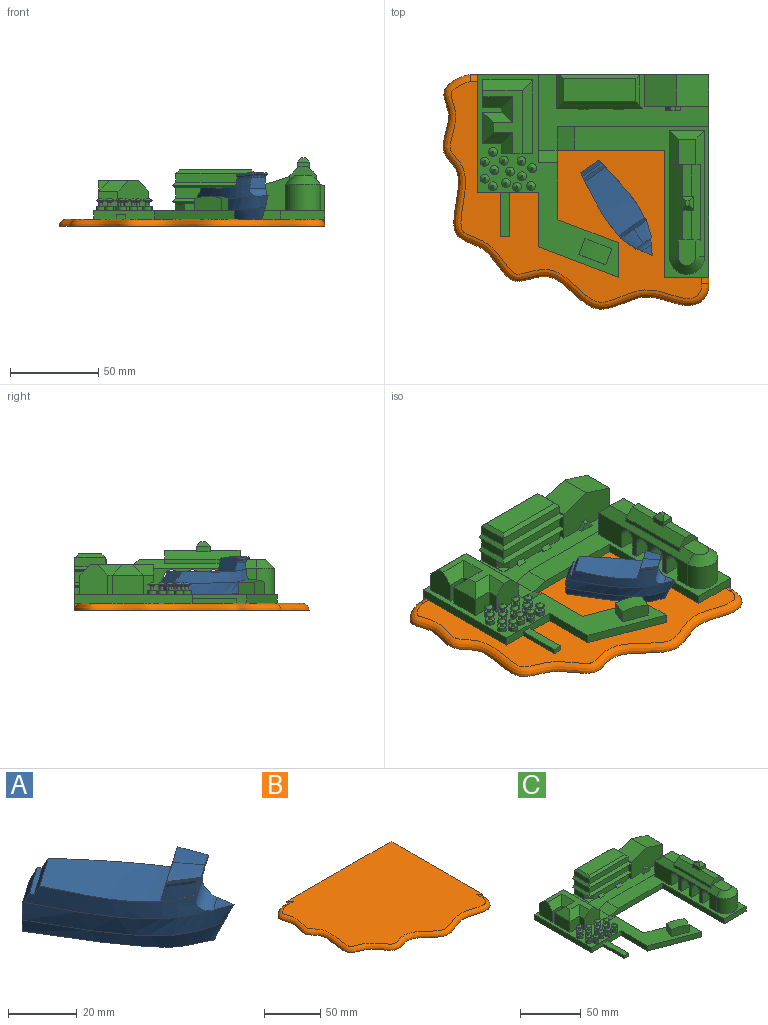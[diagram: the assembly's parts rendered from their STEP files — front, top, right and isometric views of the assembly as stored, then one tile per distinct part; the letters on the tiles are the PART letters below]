
ASSEMBLY  parts=3 mates=4
PART A: 27 faces, bbox 44x56.7x27 mm
  f0: extruded ~48.69x42.18mm, area 653.8mm2, adj f1,f2,f8,f15,f18,f19,f20
  f1: extruded ~10.02x5.16mm, area 44.1mm2, adj f0,f8,f13,f14,f15
  f2: extruded ~44.76x29.14mm, area 304.2mm2, adj f0,f3,f8,f9,f16,f17,f18
  f3: bspline ~54.16x30.25mm, area 415.7mm2, adj f2,f4,f6,f7,f9,f17,f21
  f4: bspline ~51.91x29.86mm, area 327mm2, adj f3,f5,f6,f22
  f5: plane 49.08x36.66mm, normal (0,0,-1), area 618.9mm2, adj f4,f6,f22
  f6: plane 10.3x10.22mm, normal (-0.57,0.82,0), area 123.4mm2, adj f3,f4,f5,f17,f21,f22
  f7: extruded ~8.5x8.26mm, area 17.4mm2, adj f3,f9,f21
  f8: plane 9.48x6.67mm, normal (0.57,-0.82,0), area 63.7mm2, adj f0,f1,f2,f9,f13,f19,f20,f25
  f9: cylinder r=4.5mm len=12.18mm, axis (-0.82,-0.57,0), area 70.7mm2, adj f2,f3,f7,f8,f20,f21
  f10: plane 9.4x6.6mm, normal (0.57,-0.82,0), area 9.7mm2, adj f11,f12,f13,f23,f24,f25
  f11: bspline ~13.1x10.25mm, area 70.7mm2, adj f10,f12,f15,f23
  f12: plane 10.05x3mm, normal (0.96,0.29,0), area 8.3mm2, adj f10,f11,f14,f15
  f13: bspline ~6.43x5.17mm, area 16.8mm2, adj f1,f8,f10,f14,f25
  f14: bspline ~10.67x3.88mm, area 18.7mm2, adj f1,f12,f13,f15
  f15: plane 15.46x11.63mm, normal (-0.56,0.79,0.25), area 138.5mm2, adj f0,f1,f11,f12,f14,f19,f23,f24
  f16: plane 11.87x8.91mm, normal (0,0,1), area 19.2mm2, adj f2,f17,f18,f20
  f17: plane 11.89x9.26mm, normal (-0.51,0.73,0.45), area 65mm2, adj f2,f3,f6,f16,f20,f21
  f18: plane 12.46x9.45mm, normal (-0.51,0.73,0.45), area 54.1mm2, adj f0,f2,f16,f20
  f19: extruded ~8.43x6.13mm, area 44.1mm2, adj f0,f8,f15,f25,f26
  f20: extruded ~42.69x32.09mm, area 304.2mm2, adj f0,f8,f9,f16,f17,f18,f21
  f21: bspline ~46.95x40.55mm, area 415.7mm2, adj f3,f6,f7,f9,f17,f20,f22
  f22: bspline ~45.06x39.16mm, area 327mm2, adj f4,f5,f6,f21
  f23: bspline ~12.9x11.24mm, area 70.7mm2, adj f10,f11,f15,f24
  f24: plane 8.42x6.26mm, normal (-0.6,-0.8,0), area 8.3mm2, adj f10,f15,f23,f26
  f25: bspline ~6.27x5.23mm, area 16.7mm2, adj f8,f10,f13,f19,f26
  f26: bspline ~9.37x7.07mm, area 18.5mm2, adj f15,f19,f24,f25
PART B: 9 faces, bbox 153.8x135.9x5.9 mm
  f0: plane 5.47x5.47mm, normal (-0.66,-0.75,0), area 4.6mm2, adj f1,f4,f6
  f1: plane 146.8x128.87mm, normal (0,0,1), area 16367.4mm2, adj f0,f2,f3,f4,f6,f7,f8
  f2: plane 6.5x5.92mm, normal (-0.66,-0.75,0), area 5.2mm2, adj f1,f3,f7
  f3: plane 131.21x4mm, normal (0,1,0), area 524.9mm2, adj f1,f2,f4,f5
  f4: plane 114.76x4mm, normal (1,0,0), area 459mm2, adj f0,f1,f3,f5
  f5: plane 151.91x133.98mm, normal (0,0,-1), area 17455.2mm2, adj f3,f4,f6,f7,f8
  f6: cylinder r=4mm len=6.98mm, axis (0,1,0), area 32.8mm2, adj f0,f1,f5,f8
  f7: cylinder r=4mm len=8.72mm, axis (1,0,0), area 40.4mm2, adj f1,f2,f5,f8
  f8: bspline ~150.81x132.87mm, area 1645.3mm2, adj f1,f5,f6,f7
PART C: 222 faces, bbox 131.2x114.8x35 mm
  f0: plane 25x5.22mm, normal (0,0,1), area 130.4mm2, adj f1,f3,f4,f5
  f1: plane 25x2.74mm, normal (-1,0,0), area 68.5mm2, adj f0,f2,f4,f5
  f2: plane 131.21x114.76mm, normal (0,0,-1), area 9680.6mm2, adj f1,f3,f4,f5,f14,f18,f19,f21
  f3: plane 25x2.74mm, normal (1,0,0), area 68.5mm2, adj f0,f2,f4,f5
  f4: plane 5.22x2.74mm, normal (0,-1,0), area 14.3mm2, adj f0,f1,f2,f3
  f5: plane 34.32x5mm, normal (0,-1,0), area 157.3mm2, adj f0,f1,f2,f3,f21,f27,f28
  f6: plane 9.07x6.93mm, normal (0.93,-0.35,0), area 67.2mm2, adj f7,f28,f40,f221
  f7: plane 15.35x8mm, normal (-0.35,-0.93,0), area 125.5mm2, adj f6,f28,f41,f221
  f8: plane 17.31x6mm, normal (-1,0,0), area 103.9mm2, adj f9,f14,f198,f204
  f9: plane 45.1x6mm, normal (0,-1,0), area 270.6mm2, adj f8,f10,f199,f205
  f10: plane 17.31x6mm, normal (1,0,0), area 103.9mm2, adj f9,f14,f200,f206
  f11: plane 16.56x6.5mm, normal (-1,0,0), area 82.2mm2, adj f14,f20,f203,f207,f212
  f12: plane 44.35x6.5mm, normal (0,-1,0), area 240.3mm2, adj f13,f20,f202,f207,f212,f213,f214,f215
  f13: plane 17.31x6.5mm, normal (1,0,0), area 112.5mm2, adj f12,f14,f20,f201
  f14: plane 131.21x26mm, normal (0,1,0), area 2190.5mm2, adj f2,f8,f10,f11,f13,f18,f20,f26
  f15: plane 71.57x15mm, normal (1,0,0), area 604.2mm2, adj f43,f56,f58,f63,f81,f82,f83,f84
  f16: plane 16.99x4.99mm, normal (0,0,1), area 84.8mm2, adj f48,f53,f67,f68
  f17: plane 14.6x9.99mm, normal (0,0,1), area 145.8mm2, adj f51,f63,f65,f66
  f18: plane 114.76x19mm, normal (1,0,0), area 794.4mm2, adj f2,f14,f20,f42,f43,f45,f60,f186
  f19: plane 60.93x5mm, normal (0,-1,0), area 291.5mm2, adj f2,f25,f43,f44,f61,f62
  f20: plane 96.9x42.81mm, normal (0,0,1), area 1511.6mm2, adj f11,f12,f13,f14,f18,f26,f42,f60
  f21: plane 30.82x5mm, normal (-1,0,0), area 154.1mm2, adj f2,f5,f22,f28
  f22: plane 45.51x17.26mm, normal (-0.35,-0.93,0), area 243.4mm2, adj f2,f21,f23,f28
  f23: plane 19.59x5mm, normal (1,0,0), area 97.9mm2, adj f2,f22,f24,f28
  f24: plane 34.47x13.08mm, normal (0.35,0.93,0), area 184.3mm2, adj f2,f23,f25,f28
  f25: plane 39.29x5mm, normal (1,0,0), area 187.7mm2, adj f2,f19,f24,f28,f62
  f26: plane 49.81x2.5mm, normal (1,0,0), area 115.8mm2, adj f14,f20,f28,f62
  f27: plane 66.67x5mm, normal (-1,0,0), area 333.4mm2, adj f2,f5,f14,f28
  f28: plane 114.76x79.83mm, normal (0,0,1), area 2011.8mm2, adj f5,f6,f7,f14,f21,f22,f23,f24
  f29: plane 17x15.69mm, normal (-1,0,0), area 230.7mm2, adj f28,f30,f38,f39,f74,f75
  f30: plane 11x10.83mm, normal (0,-1,0), area 119.1mm2, adj f28,f29,f31,f75
  f31: plane 11x2.65mm, normal (-1,0,0), area 29.2mm2, adj f28,f30,f32,f76
  f32: plane 11x10.83mm, normal (0,1,0), area 119.1mm2, adj f28,f31,f33,f77
  f33: plane 17.5x11mm, normal (-1,0,0), area 192.5mm2, adj f28,f32,f34,f78
  f34: plane 11x10.83mm, normal (0,-1,0), area 119.1mm2, adj f28,f33,f35,f79
  f35: plane 11x5.92mm, normal (-1,0,0), area 65.2mm2, adj f28,f34,f36,f80
  f36: plane 17.4x17mm, normal (0,-1,0), area 259.8mm2, adj f28,f35,f37,f39,f73,f80
  f37: plane 41.76x11mm, normal (1,0,0), area 459.4mm2, adj f28,f36,f38,f73
  f38: plane 28.23x11mm, normal (0,1,0), area 310.5mm2, adj f28,f29,f37,f74
  f39: plane 35.76x22.23mm, normal (0,0,1), area 314.8mm2, adj f29,f36,f73,f74,f75,f76,f77,f78
  f40: plane 15.35x8mm, normal (0.35,0.93,0), area 125.5mm2, adj f6,f28,f41,f221
  f41: plane 9.07x6.93mm, normal (-0.93,0.35,0), area 67.2mm2, adj f7,f28,f40,f221
  f42: plane 86.13x2.5mm, normal (0,1,0), area 202.8mm2, adj f18,f20,f43,f61
  f43: plane 85.44x76.13mm, normal (0,0,1), area 1972mm2, adj f15,f18,f19,f42,f44,f45,f56,f57
  f44: plane 71.95x5mm, normal (-1,0,0), area 359.8mm2, adj f2,f19,f43,f45
  f45: plane 25.19x5mm, normal (0,-1,0), area 126mm2, adj f2,f18,f43,f44
  f46: plane 7x3.7mm, normal (0,1,0), area 18.5mm2, adj f47,f49,f55,f67,f68,f70
  f47: plane 7.8x3.3mm, normal (-1,0,0), area 25.7mm2, adj f46,f48,f68,f69
  f48: plane 7x3.7mm, normal (0,-1,0), area 18.5mm2, adj f16,f47,f49,f67,f68,f71
  f49: plane 7.8x3.7mm, normal (1,0,0), area 28.9mm2, adj f46,f48,f67,f72
  f50: plane 2.8x2mm, normal (0,0,1), area 5.6mm2, adj f69,f70,f71,f72
  f51: plane 14.99x7.6mm, normal (0,1,0), area 56.2mm2, adj f17,f52,f54,f55,f63,f66,f67,f68
  f52: plane 42.58x2.41mm, normal (-1,0,0), area 102.6mm2, adj f51,f53,f66,f68
  f53: plane 14.99x7.6mm, normal (0,-1,0), area 56.2mm2, adj f16,f52,f54,f59,f63,f66,f67,f68
  f54: plane 42.58x2.6mm, normal (1,0,0), area 110.6mm2, adj f51,f53,f63,f67
  f55: plane 17.79x4.99mm, normal (0,0,1), area 88.8mm2, adj f46,f51,f67,f68
  f56: plane 19.99x15mm, normal (0,1,0), area 299.8mm2, adj f15,f43,f57,f65
  f57: plane 71.57x15mm, normal (-1,0,0), area 604.2mm2, adj f43,f56,f58,f66,f81,f82,f83,f84
  f58: cylinder r=9.99mm len=19.99mm, axis (0,0,-1), area 470.9mm2, adj f15,f43,f57,f64
  f59: plane 14.38x9.99mm, normal (0,0,1), area 132.9mm2, adj f53,f63,f64,f66
  f60: plane 36.38x22.24mm, normal (0,-1,0), area 682.3mm2, adj f18,f20,f184,f185,f186,f209,f210,f211
  f61: plane 13.49x10mm, normal (-0.24,0,0.97), area 139mm2, adj f19,f20,f42,f43
  f62: plane 11.04x7mm, normal (0,0.34,0.94), area 82mm2, adj f19,f20,f25,f26,f28
  f63: plane 71.57x5mm, normal (0.71,0,0.71), area 332mm2, adj f15,f17,f51,f53,f54,f59,f64,f65
  f64: cone r=4.99mm half-angle=45deg, axis (0,0,-1), area 166.5mm2, adj f58,f59,f63,f66
  f65: plane 19.99x5mm, normal (0,0.71,0.71), area 106mm2, adj f17,f56,f63,f66
  f66: plane 71.57x5mm, normal (-0.71,0,0.71), area 343.3mm2, adj f17,f51,f52,f53,f57,f59,f64,f65
  f67: plane 42.58x5mm, normal (0.71,0,0.71), area 287.8mm2, adj f16,f46,f48,f49,f51,f53,f54,f55
  f68: plane 42.58x5mm, normal (-0.71,0,0.71), area 292.2mm2, adj f16,f46,f47,f48,f51,f52,f53,f55
  f69: plane 7.8x2.5mm, normal (-0.71,0,0.71), area 18.7mm2, adj f47,f50,f70,f71
  f70: plane 7x2.5mm, normal (0,0.71,0.71), area 15.9mm2, adj f46,f50,f69,f72
  f71: plane 7x2.5mm, normal (0,-0.71,0.71), area 15.9mm2, adj f48,f50,f69,f72
  f72: plane 7.8x2.5mm, normal (0.71,0,0.71), area 18.7mm2, adj f49,f50,f70,f71
  f73: plane 41.76x6mm, normal (0.71,0,0.71), area 328.9mm2, adj f36,f37,f39,f74
  f74: plane 28.23x6mm, normal (0,0.71,0.71), area 214.1mm2, adj f29,f38,f39,f73
  f75: plane 16.83x6mm, normal (0,-0.71,0.71), area 117.3mm2, adj f29,f30,f39,f76
  f76: plane 14.65x6mm, normal (-0.71,0,0.71), area 73.4mm2, adj f31,f39,f75,f77
  f77: plane 16.83x6mm, normal (0,0.71,0.71), area 91.9mm2, adj f32,f39,f76,f78
  f78: plane 17.5x6mm, normal (-0.71,0,0.71), area 97.6mm2, adj f33,f39,f77,f79
  f79: plane 16.83x6mm, normal (0,-0.71,0.71), area 91.9mm2, adj f34,f39,f78,f80
  f80: plane 11.92x6mm, normal (-0.71,0,0.71), area 75.7mm2, adj f35,f36,f39,f79
  f81: plane 19.99x9.5mm, normal (0,1,0), area 189.9mm2, adj f15,f43,f57,f83
  f82: plane 19.99x9.5mm, normal (0,-1,0), area 189.9mm2, adj f15,f43,f57,f83
  f83: cylinder r=4.5mm len=19.99mm, axis (1,0,0), area 282.6mm2, adj f15,f57,f81,f82
  f84: plane 19.99x9.5mm, normal (0,1,0), area 189.9mm2, adj f15,f43,f57,f86
  f85: plane 19.99x9.5mm, normal (0,-1,0), area 189.9mm2, adj f15,f43,f57,f86
  f86: cylinder r=4.5mm len=19.99mm, axis (1,0,0), area 282.6mm2, adj f15,f57,f84,f85
  f87: plane 19.99x9.5mm, normal (0,1,0), area 189.9mm2, adj f15,f43,f57,f89
  f88: plane 19.99x9.5mm, normal (0,-1,0), area 189.9mm2, adj f15,f43,f57,f89
  f89: cylinder r=4.5mm len=19.99mm, axis (1,0,0), area 282.6mm2, adj f15,f57,f87,f88
  f90: plane 19.99x9.5mm, normal (0,-1,0), area 189.9mm2, adj f15,f43,f57,f91
  f91: cylinder r=4.5mm len=19.99mm, axis (1,0,0), area 282.6mm2, adj f15,f57,f90,f92
  f92: plane 19.99x9.5mm, normal (0,1,0), area 189.9mm2, adj f15,f43,f57,f91
  f93: cylinder r=2.5mm len=5mm, axis (0,0,-1), area 39.3mm2, adj f28,f94
  f94: plane 5x5mm, normal (0,0,1), area 16.5mm2, adj f93,f99
  f95: plane 1x1mm, normal (0,0,1), area 0.8mm2, adj f96
  f96: cone r=0.5mm half-angle=53.1deg, axis (0,0,-1), area 23.6mm2, adj f95,f97
  f97: plane 5x5mm, normal (0,0,-1), area 7.1mm2, adj f96,f98
  f98: cone r=1mm half-angle=45deg, axis (0,0,1), area 13.3mm2, adj f97,f99
  f99: cylinder r=1mm len=2mm, axis (0,0,-1), area 12.6mm2, adj f94,f98
  f100: cylinder r=2.5mm len=5mm, axis (0,0,-1), area 39.3mm2, adj f28,f101
  f101: plane 5x5mm, normal (0,0,1), area 16.5mm2, adj f100,f106
  f102: plane 1x1mm, normal (0,0,1), area 0.8mm2, adj f103
  f103: cone r=0.5mm half-angle=53.1deg, axis (0,0,-1), area 23.6mm2, adj f102,f104
  f104: plane 5x5mm, normal (0,0,-1), area 7.1mm2, adj f103,f105
  f105: cone r=1mm half-angle=45deg, axis (0,0,1), area 13.3mm2, adj f104,f106
  f106: cylinder r=1mm len=2mm, axis (0,0,-1), area 12.6mm2, adj f101,f105
  f107: cylinder r=2.5mm len=5mm, axis (0,0,-1), area 39.3mm2, adj f28,f108
  f108: plane 5x5mm, normal (0,0,1), area 16.5mm2, adj f107,f113
  f109: plane 1x1mm, normal (0,0,1), area 0.8mm2, adj f110
  f110: cone r=0.5mm half-angle=53.1deg, axis (0,0,-1), area 23.6mm2, adj f109,f111
  f111: plane 5x5mm, normal (0,0,-1), area 7.1mm2, adj f110,f112
  f112: cone r=1mm half-angle=45deg, axis (0,0,1), area 13.3mm2, adj f111,f113
  f113: cylinder r=1mm len=2mm, axis (0,0,-1), area 12.6mm2, adj f108,f112
  f114: cylinder r=2.5mm len=5mm, axis (0,0,-1), area 39.3mm2, adj f28,f115
  f115: plane 5x5mm, normal (0,0,1), area 16.5mm2, adj f114,f120
  f116: plane 1x1mm, normal (0,0,1), area 0.8mm2, adj f117
  f117: cone r=0.5mm half-angle=53.1deg, axis (0,0,-1), area 23.6mm2, adj f116,f118
  f118: plane 5x5mm, normal (0,0,-1), area 7.1mm2, adj f117,f119
  f119: cone r=1mm half-angle=45deg, axis (0,0,1), area 13.3mm2, adj f118,f120
  f120: cylinder r=1mm len=2mm, axis (0,0,-1), area 12.6mm2, adj f115,f119
  f121: cylinder r=2.5mm len=5mm, axis (0,0,-1), area 39.3mm2, adj f28,f122
  f122: plane 5x5mm, normal (0,0,1), area 16.5mm2, adj f121,f127
  f123: plane 1x1mm, normal (0,0,1), area 0.8mm2, adj f124
  f124: cone r=0.5mm half-angle=53.1deg, axis (0,0,-1), area 23.6mm2, adj f123,f125
  f125: plane 5x5mm, normal (0,0,-1), area 7.1mm2, adj f124,f126
  f126: cone r=1mm half-angle=45deg, axis (0,0,1), area 13.3mm2, adj f125,f127
  f127: cylinder r=1mm len=2mm, axis (0,0,-1), area 12.6mm2, adj f122,f126
  f128: cylinder r=2.5mm len=5mm, axis (0,0,-1), area 39.3mm2, adj f28,f129
  f129: plane 5x5mm, normal (0,0,1), area 16.5mm2, adj f128,f134
  f130: plane 1x1mm, normal (0,0,1), area 0.8mm2, adj f131
  f131: cone r=0.5mm half-angle=53.1deg, axis (0,0,-1), area 23.6mm2, adj f130,f132
  f132: plane 5x5mm, normal (0,0,-1), area 7.1mm2, adj f131,f133
  f133: cone r=1mm half-angle=45deg, axis (0,0,1), area 13.3mm2, adj f132,f134
  f134: cylinder r=1mm len=2mm, axis (0,0,-1), area 12.6mm2, adj f129,f133
  f135: cylinder r=2.5mm len=5mm, axis (0,0,-1), area 39.3mm2, adj f28,f136
  f136: plane 5x5mm, normal (0,0,1), area 16.5mm2, adj f135,f141
  f137: plane 1x1mm, normal (0,0,1), area 0.8mm2, adj f138
  f138: cone r=0.5mm half-angle=53.1deg, axis (0,0,-1), area 23.6mm2, adj f137,f139
  f139: plane 5x5mm, normal (0,0,-1), area 7.1mm2, adj f138,f140
  f140: cone r=1mm half-angle=45deg, axis (0,0,1), area 13.3mm2, adj f139,f141
  f141: cylinder r=1mm len=2mm, axis (0,0,-1), area 12.6mm2, adj f136,f140
  f142: cylinder r=2.5mm len=5mm, axis (0,0,-1), area 39.3mm2, adj f28,f143
  f143: plane 5x5mm, normal (0,0,1), area 16.5mm2, adj f142,f148
  f144: plane 1x1mm, normal (0,0,1), area 0.8mm2, adj f145
  f145: cone r=0.5mm half-angle=53.1deg, axis (0,0,-1), area 23.6mm2, adj f144,f146
  f146: plane 5x5mm, normal (0,0,-1), area 7.1mm2, adj f145,f147
  f147: cone r=1mm half-angle=45deg, axis (0,0,1), area 13.3mm2, adj f146,f148
  f148: cylinder r=1mm len=2mm, axis (0,0,-1), area 12.6mm2, adj f143,f147
  f149: cylinder r=2.5mm len=5mm, axis (0,0,-1), area 39.3mm2, adj f28,f150
  f150: plane 5x5mm, normal (0,0,1), area 16.5mm2, adj f149,f155
  f151: plane 1x1mm, normal (0,0,1), area 0.8mm2, adj f152
  f152: cone r=0.5mm half-angle=53.1deg, axis (0,0,-1), area 23.6mm2, adj f151,f153
  f153: plane 5x5mm, normal (0,0,-1), area 7.1mm2, adj f152,f154
  f154: cone r=1mm half-angle=45deg, axis (0,0,1), area 13.3mm2, adj f153,f155
  f155: cylinder r=1mm len=2mm, axis (0,0,-1), area 12.6mm2, adj f150,f154
  f156: cylinder r=2.5mm len=5mm, axis (0,0,-1), area 39.3mm2, adj f28,f157
  f157: plane 5x5mm, normal (0,0,1), area 16.5mm2, adj f156,f162
  f158: plane 1x1mm, normal (0,0,1), area 0.8mm2, adj f159
  f159: cone r=0.5mm half-angle=53.1deg, axis (0,0,-1), area 23.6mm2, adj f158,f160
  f160: plane 5x5mm, normal (0,0,-1), area 7.1mm2, adj f159,f161
  f161: cone r=1mm half-angle=45deg, axis (0,0,1), area 13.3mm2, adj f160,f162
  f162: cylinder r=1mm len=2mm, axis (0,0,-1), area 12.6mm2, adj f157,f161
  f163: cylinder r=2.5mm len=5mm, axis (0,0,-1), area 39.3mm2, adj f28,f164
  f164: plane 5x5mm, normal (0,0,1), area 16.5mm2, adj f163,f169
  f165: plane 1x1mm, normal (0,0,1), area 0.8mm2, adj f166
  f166: cone r=0.5mm half-angle=53.1deg, axis (0,0,-1), area 23.6mm2, adj f165,f167
  f167: plane 5x5mm, normal (0,0,-1), area 7.1mm2, adj f166,f168
  f168: cone r=1mm half-angle=45deg, axis (0,0,1), area 13.3mm2, adj f167,f169
  f169: cylinder r=1mm len=2mm, axis (0,0,-1), area 12.6mm2, adj f164,f168
  f170: cylinder r=2.5mm len=5mm, axis (0,0,-1), area 39.3mm2, adj f28,f171
  f171: plane 5x5mm, normal (0,0,1), area 16.5mm2, adj f170,f176
  f172: plane 1x1mm, normal (0,0,1), area 0.8mm2, adj f173
  f173: cone r=0.5mm half-angle=53.1deg, axis (0,0,-1), area 23.6mm2, adj f172,f174
  f174: plane 5x5mm, normal (0,0,-1), area 7.1mm2, adj f173,f175
  f175: cone r=1mm half-angle=45deg, axis (0,0,1), area 13.3mm2, adj f174,f176
  f176: cylinder r=1mm len=2mm, axis (0,0,-1), area 12.6mm2, adj f171,f175
  f177: cylinder r=2.5mm len=5mm, axis (0,0,-1), area 39.3mm2, adj f28,f178
  f178: plane 5x5mm, normal (0,0,1), area 16.5mm2, adj f177,f183
  f179: plane 1x1mm, normal (0,0,1), area 0.8mm2, adj f180
  f180: cone r=0.5mm half-angle=53.1deg, axis (0,0,-1), area 23.6mm2, adj f179,f181
  f181: plane 5x5mm, normal (0,0,-1), area 7.1mm2, adj f180,f182
  f182: cone r=1mm half-angle=45deg, axis (0,0,1), area 13.3mm2, adj f181,f183
  f183: cylinder r=1mm len=2mm, axis (0,0,-1), area 12.6mm2, adj f178,f182
  f184: plane 17.81x16.5mm, normal (-1,0,0), area 293.9mm2, adj f14,f20,f60,f185
  f185: plane 18.19x17.81mm, normal (-0.3,0,0.95), area 339.8mm2, adj f14,f60,f184,f186
  f186: plane 18.19x17.81mm, normal (0.3,0,0.95), area 339.8mm2, adj f14,f18,f60,f185
  f187: plane 17.31x5mm, normal (-1,0,0), area 86.6mm2, adj f14,f188,f192,f195
  f188: plane 45.1x5mm, normal (0,-1,0), area 225.5mm2, adj f187,f189,f191,f196
  f189: plane 17.31x5mm, normal (1,0,0), area 86.6mm2, adj f14,f188,f193,f197
  f190: plane 41.1x13.31mm, normal (0,0,1), area 547.2mm2, adj f191,f192,f193,f194
  f191: plane 45.1x2mm, normal (0,-0.71,0.71), area 121.9mm2, adj f188,f190,f192,f193
  f192: plane 17.31x2mm, normal (-0.71,0,0.71), area 43.3mm2, adj f187,f190,f191,f194
  f193: plane 17.31x2mm, normal (0.71,0,0.71), area 43.3mm2, adj f189,f190,f191,f194
  f194: plane 45.1x2mm, normal (0,0.71,0.71), area 121.9mm2, adj f14,f190,f192,f193
  f195: plane 19.31x2mm, normal (-0.71,0,0.71), area 51.8mm2, adj f14,f187,f196,f204
  f196: plane 49.1x2mm, normal (0,-0.71,0.71), area 133.2mm2, adj f188,f195,f197,f205
  f197: plane 19.31x2mm, normal (0.71,0,0.71), area 51.8mm2, adj f14,f189,f196,f206
  f198: plane 19.31x2mm, normal (-0.71,0,0.71), area 51.8mm2, adj f8,f14,f199,f203
  f199: plane 49.1x2mm, normal (0,-0.71,0.71), area 133.2mm2, adj f9,f198,f200,f202
  f200: plane 19.31x2mm, normal (0.71,0,0.71), area 51.8mm2, adj f10,f14,f199,f201
  f201: plane 19.31x2mm, normal (0.45,0,-0.89), area 40.9mm2, adj f13,f14,f200,f202
  f202: plane 49.1x4.5mm, normal (0,-0.45,-0.89), area 112.3mm2, adj f12,f199,f201,f203,f207
  f203: plane 19.31x4.5mm, normal (-0.45,0,-0.89), area 47.9mm2, adj f11,f14,f198,f202,f207
  f204: plane 19.31x2mm, normal (-0.45,0,-0.89), area 40.9mm2, adj f8,f14,f195,f205
  f205: plane 49.1x2mm, normal (0,-0.45,-0.89), area 105.3mm2, adj f9,f196,f204,f206
  f206: plane 19.31x2mm, normal (0.45,0,-0.89), area 40.9mm2, adj f10,f14,f197,f205
  f207: plane 5.5x5mm, normal (-0.71,-0.71,0), area 34.5mm2, adj f11,f12,f202,f203,f212
  f208: plane 8.6x4mm, normal (0,-1,0), area 22.4mm2, adj f20,f209,f210,f211
  f209: plane 2.6x2.58mm, normal (0,0,1), area 6.7mm2, adj f60,f208,f210,f211
  f210: plane 4x3mm, normal (-0.8,0,0.6), area 12.9mm2, adj f20,f60,f208,f209
  f211: plane 4x3mm, normal (0.8,0,0.6), area 12.9mm2, adj f20,f60,f208,f209
  f212: plane 5x5mm, normal (-0.22,-0.22,0.95), area 12.9mm2, adj f11,f12,f20,f207
  f213: plane 2.08x2mm, normal (-1,0,0), area 2.2mm2, adj f12,f20,f215,f220
  f214: plane 2.08x2mm, normal (1,0,0), area 2.2mm2, adj f12,f20,f215,f220
  f215: plane 5.4x0.08mm, normal (0,0,1), area 0.4mm2, adj f12,f213,f214,f220
  f216: plane 2.08x2mm, normal (-1,0,0), area 2.2mm2, adj f12,f20,f218,f219
  f217: plane 2.08x2mm, normal (1,0,0), area 2.2mm2, adj f12,f20,f218,f219
  f218: plane 5.86x0.08mm, normal (0,0,1), area 0.5mm2, adj f12,f216,f217,f219
  f219: plane 5.86x2mm, normal (0,-0.71,0.71), area 16.6mm2, adj f20,f216,f217,f218
  f220: plane 5.4x2mm, normal (0,-0.71,0.71), area 15.3mm2, adj f20,f213,f214,f215
  f221: cylinder r=31.91mm len=18.79mm, axis (-0.35,-0.93,0), area 161.1mm2, adj f6,f7,f40,f41
PLACE A t=(-77.99,75.3,-52.84)mm
PLACE B t=(-20.55,-26.48,-16.54)mm
PLACE C t=(-20.55,-26.48,-16.54)mm
MATE planar C.f18 <-> B.f4  axis (1,0,0) through (65.3,46.71,-2.54)mm
MATE planar B.f1 <-> A.f5  axis (0,0,1) through (-2.16,-2.63,-21.54)mm
MATE planar C.f14 <-> B.f3  axis (0,1,0) through (14.82,55.61,-10.29)mm
MATE planar C.f2 <-> B.f1  axis (0,0,-1) through (65.3,-1.77,-21.54)mm
